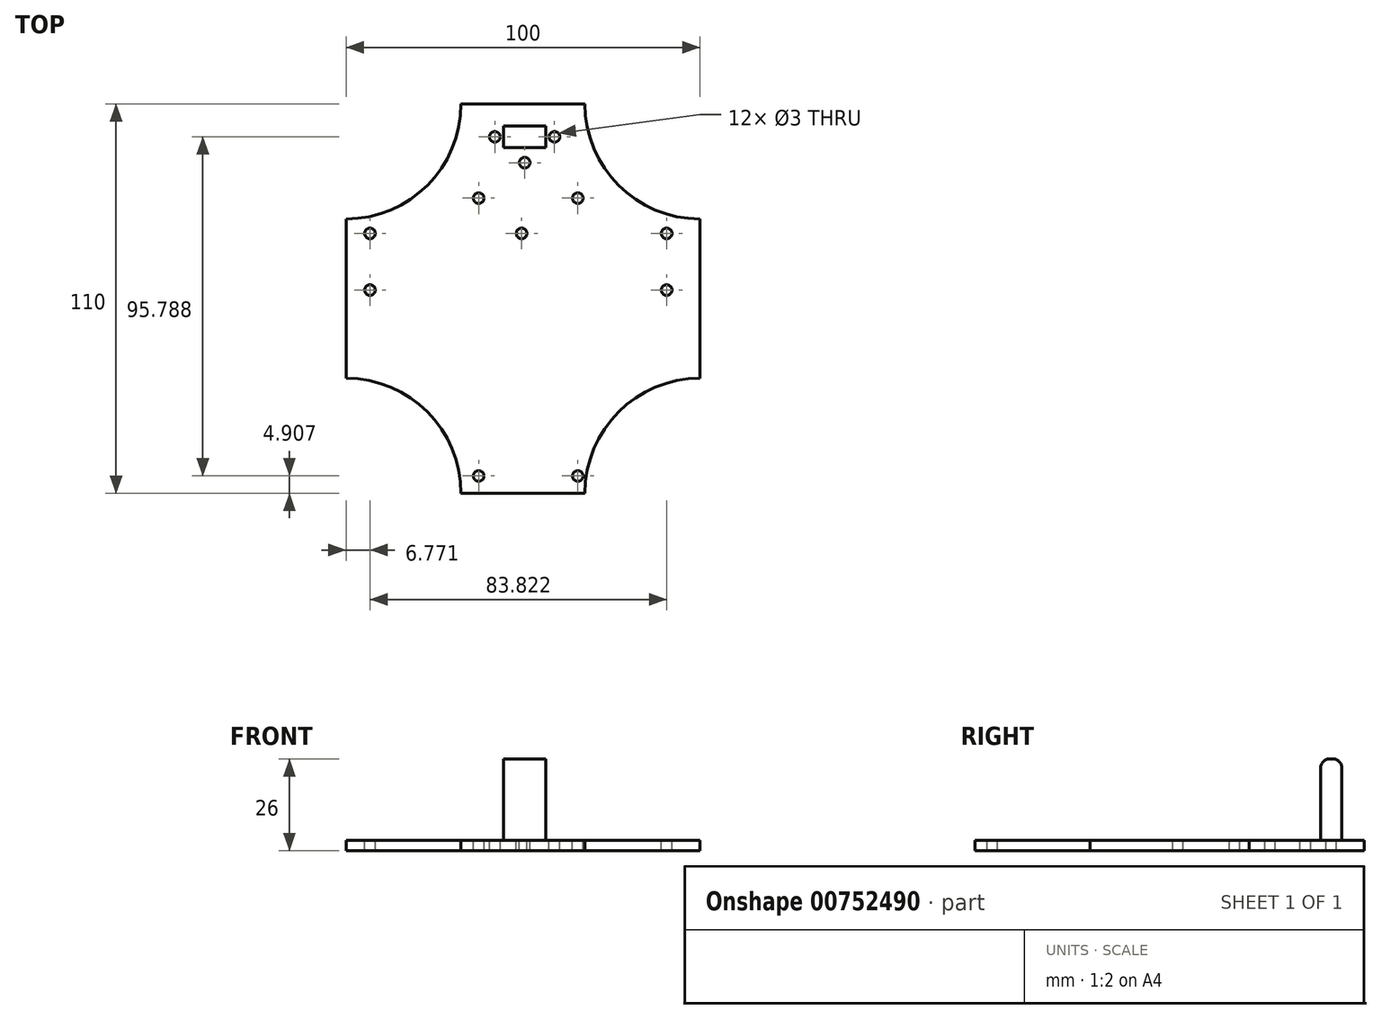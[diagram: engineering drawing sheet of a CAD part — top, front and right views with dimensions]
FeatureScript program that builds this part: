
annotation { "Feature Type Name" : "Feature", "Feature Type Description" : "" }
export const myFeature = defineFeature(function(context is Context, id is Id, definition is map)
    precondition{}
    {
        {
            var Q0;
            Q0=qCreatedBy(makeId("Top.planeOp"),FACE);
            var sketch = newSketch(context, id + "F0", { "sketchPlane" : qUnion([Q0])});
            skLineSegment(sketch, "E0.bottom", {"start": v(-68.37, 110) * mm, "end": v(31.63, 110) * mm});
            skLineSegment(sketch, "E0.top", {"start": v(-68.37, 0) * mm, "end": v(31.63, 0) * mm});
            skLineSegment(sketch, "E0.left", {"start": v(-68.37, 110) * mm, "end": v(-68.37, 0) * mm});
            skLineSegment(sketch, "E0.right", {"start": v(31.63, 110) * mm, "end": v(31.63, 0) * mm});
            skCircle(sketch, "E1", {"center": v(-68.37, 110) * mm, "radius": 32.5 * mm});
            skCircle(sketch, "E2", {"center": v(31.63, 110) * mm, "radius": 32.5 * mm});
            skCircle(sketch, "E3", {"center": v(31.63, 0) * mm, "radius": 32.5 * mm});
            skCircle(sketch, "E4", {"center": v(-68.37, 0) * mm, "radius": 32.5 * mm});
            skSolve(sketch);
        }
        {
            var Q0;
            {var subQ5=sQuery(id+"F0.wireOp",EDGE,"E1");var subQ13=sQuery(id+"F0.wireOp",EDGE,"E0.bottom");var subQ14=makeQuery(id+"F0.imprint","INTERSECT",VERTEX,{"derivedFrom":[subQ13,subQ5]});Q0=makeQuery(id+"F0.imprint","IMPRINT",FACE,{"disambiguationData":[TD([[makeQuery(id+"F0.imprint","IMPRINT",EDGE,{"disambiguationData":[TD([[subQ14,-1.0]])],"derivedFrom":subQ13}),-1.0]])]});}
            extrude(context, id + "F1", {"entities" : qUnion([Q0]), "oppositeDirection" : true, "depth" : 3 * mm, "offsetDistance" : 25 * mm});
        }
        {
            var Q0;
            Q0=makeQuery(id+"F1.opExtrude","CAP_FACE",FACE,{"disambiguationData":[OSD([sQuery(id+"F0.wireOp",EDGE,"E0.bottom"),sQuery(id+"F0.wireOp",EDGE,"E0.top"),sQuery(id+"F0.wireOp",EDGE,"E0.left"),sQuery(id+"F0.wireOp",EDGE,"E0.right"),sQuery(id+"F0.wireOp",EDGE,"E1"),sQuery(id+"F0.wireOp",EDGE,"E2"),sQuery(id+"F0.wireOp",EDGE,"E3"),sQuery(id+"F0.wireOp",EDGE,"E4")])],"isStart":true});
            var sketch = newSketch(context, id + "F2", { "sketchPlane" : qUnion([Q0])});
            skLineSegment(sketch, "E5.bottom", {"start": v(-11.9, 97.7) * mm, "end": v(-23.9, 97.7) * mm});
            skLineSegment(sketch, "E5.top", {"start": v(-11.9, 103.7) * mm, "end": v(-23.9, 103.7) * mm});
            skLineSegment(sketch, "E5.left", {"start": v(-11.9, 97.7) * mm, "end": v(-11.9, 103.7) * mm});
            skLineSegment(sketch, "E5.right", {"start": v(-23.9, 97.7) * mm, "end": v(-23.9, 103.7) * mm});
            skSolve(sketch);
        }
        {
            var Q0;
            Q0 = qSketchRegion(id + "F2", true);
            extrude(context, id + "F3", {"entities" : qUnion([Q0]), "operationType" : NewBodyOperationType.ADD, "depth" : 23 * mm, "offsetDistance" : 25 * mm});
        }
        {
            var Q0;
            Q0=makeQuery(id+"F3.opExtrude","CAP_EDGE",EDGE,{"disambiguationData":[OSD([sQuery(id+"F2.wireOp",EDGE,"E5.top")])],"isStart":false});
            var Q1;
            Q1=makeQuery(id+"F3.opExtrude","CAP_EDGE",EDGE,{"disambiguationData":[OSD([sQuery(id+"F2.wireOp",EDGE,"E5.bottom")])],"isStart":false});
            fillet(context, id + "F4", {"entities" : qUnion([Q0, Q1]), "radius" : 2.66 * mm, "tangentPropagation" : true, "allowEdgeOverflow" : false});
        }
        {
            var Q0;
            Q0=makeQuery(id+"F1.opExtrude","CAP_FACE",FACE,{"disambiguationData":[OSD([sQuery(id+"F0.wireOp",EDGE,"E0.bottom"),sQuery(id+"F0.wireOp",EDGE,"E0.top"),sQuery(id+"F0.wireOp",EDGE,"E0.left"),sQuery(id+"F0.wireOp",EDGE,"E0.right"),sQuery(id+"F0.wireOp",EDGE,"E1"),sQuery(id+"F0.wireOp",EDGE,"E2"),sQuery(id+"F0.wireOp",EDGE,"E3"),sQuery(id+"F0.wireOp",EDGE,"E4")])],"isStart":true});
            var sketch = newSketch(context, id + "F5", { "sketchPlane" : qUnion([Q0])});
            skPoint(sketch, "E6.centerSnap0", {"position": v(-23.9, 100.7) * mm});
            skCircle(sketch, "E7", {"center": v(-9.49, 100.7) * mm, "radius": 1.5 * mm});
            skPoint(sketch, "E7.centerSnap0", {"position": v(-11.9, 100.7) * mm});
            skCircle(sketch, "E8", {"center": v(-26.32, 100.7) * mm, "radius": 1.5 * mm});
            skCircle(sketch, "E9", {"center": v(-17.9, 93.38) * mm, "radius": 1.5 * mm});
            skPoint(sketch, "E9.centerSnap0", {"position": v(-17.9, 97.7) * mm});
            skLineSegment(sketch, "E10", {"start": v(-17.9, 93.38) * mm, "end": v(-18.78, 73.4) * mm});
            skCircle(sketch, "E11", {"center": v(-18.78, 73.4) * mm, "radius": 1.5 * mm});
            skCircle(sketch, "E12", {"center": v(-2.89, 83.4) * mm, "radius": 1.5 * mm});
            skPoint(sketch, "E12.centerSnap0", {"position": v(-18.34, 83.4) * mm});
            skCircle(sketch, "E13", {"center": v(-30.89, 83.4) * mm, "radius": 1.5 * mm});
            skCircle(sketch, "E14", {"center": v(22.22, 73.4) * mm, "radius": 1.5 * mm});
            skCircle(sketch, "E15", {"center": v(22.22, 57.4) * mm, "radius": 1.5 * mm});
            skCircle(sketch, "E16", {"center": v(-61.6, 73.4) * mm, "radius": 1.5 * mm});
            skCircle(sketch, "E17", {"center": v(-61.6, 57.4) * mm, "radius": 1.5 * mm});
            skLineSegment(sketch, "E18", {"start": v(22.22, 57.4) * mm, "end": v(22.22, 73.4) * mm});
            skLineSegment(sketch, "E19", {"start": v(-2.89, 83.4) * mm, "end": v(-30.89, 83.4) * mm});
            skCircle(sketch, "E20", {"center": v(-2.89, 4.9) * mm, "radius": 1.5 * mm});
            skCircle(sketch, "E21", {"center": v(-30.89, 4.9) * mm, "radius": 1.5 * mm});
            skSolve(sketch);
        }
        {
            var Q0;
            Q0 = qSketchRegion(id + "F5", true);
            extrude(context, id + "F6", {"entities" : qUnion([Q0]), "operationType" : NewBodyOperationType.REMOVE, "oppositeDirection" : true, "depth" : 25 * mm, "offsetDistance" : 25 * mm});
        }
    });
